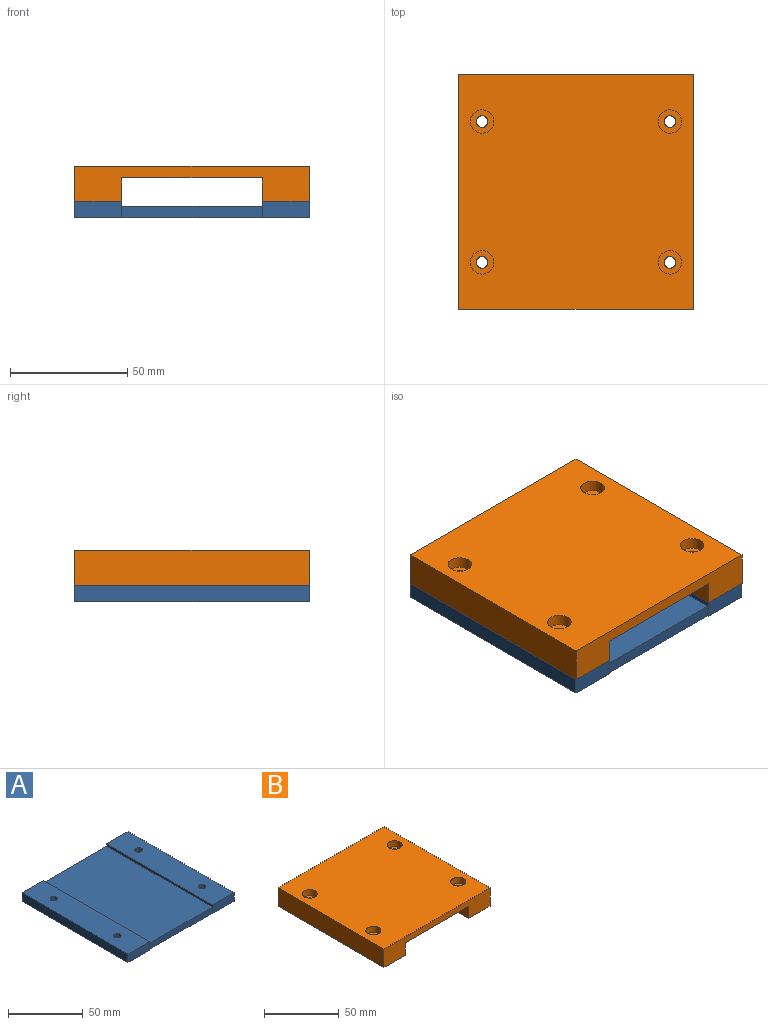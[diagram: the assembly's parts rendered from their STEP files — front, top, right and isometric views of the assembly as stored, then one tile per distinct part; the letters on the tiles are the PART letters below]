
ASSEMBLY  parts=2 mates=1
PART A: 24 faces, bbox 100x100x7 mm
  f0: plane 100x7mm, normal (0,1,0), area 580mm2, adj f2,f3,f4,f5,f7,f8,f10,f11
  f1: plane 60x5mm, normal (0,-1,0), area 300mm2, adj f2,f3,f4,f8
  f2: plane 99.46x60mm, normal (0,0,1), area 5967.6mm2, adj f0,f1,f4,f8
  f3: plane 100x100mm, normal (0,0,-1), area 9653.4mm2, adj f0,f1,f4,f5,f6,f8,f9,f10
  f4: plane 100x7mm, normal (1,0,0), area 202.7mm2, adj f0,f1,f2,f3,f6,f7
  f5: plane 100x7mm, normal (-1,0,0), area 700mm2, adj f0,f3,f6,f7
  f6: plane 20x7mm, normal (0,-1,0), area 140mm2, adj f3,f4,f5,f7
  f7: plane 100x20mm, normal (0,0,1), area 1960.7mm2, adj f0,f4,f5,f6,f12,f15
  f8: plane 100x7mm, normal (-1,0,0), area 202.7mm2, adj f0,f1,f2,f3,f9,f11
  f9: plane 20x7mm, normal (0,-1,0), area 140mm2, adj f3,f8,f10,f11
  f10: plane 100x7mm, normal (1,0,0), area 700mm2, adj f0,f3,f9,f11
  f11: plane 100x20mm, normal (0,0,1), area 1960.7mm2, adj f0,f8,f9,f10,f18,f21
  f12: cylinder r=2.5mm len=5mm, axis (0,0,-1), area 31.4mm2, adj f7,f13
  f13: plane 10x10mm, normal (0,0,-1), area 58.9mm2, adj f12,f14
  f14: cylinder r=5mm len=10mm, axis (0,0,-1), area 157.1mm2, adj f3,f13
  f15: cylinder r=2.5mm len=5mm, axis (0,0,-1), area 31.4mm2, adj f7,f16
  f16: plane 10x10mm, normal (0,0,-1), area 58.9mm2, adj f15,f17
  f17: cylinder r=5mm len=10mm, axis (0,0,-1), area 157.1mm2, adj f3,f16
  f18: cylinder r=2.5mm len=5mm, axis (0,0,-1), area 31.4mm2, adj f11,f19
  f19: plane 10x10mm, normal (0,0,-1), area 58.9mm2, adj f18,f20
  f20: cylinder r=5mm len=10mm, axis (0,0,-1), area 157.1mm2, adj f3,f19
  f21: cylinder r=2.5mm len=5mm, axis (0,0,-1), area 31.4mm2, adj f11,f22
  f22: plane 10x10mm, normal (0,0,-1), area 58.9mm2, adj f21,f23
  f23: cylinder r=5mm len=10mm, axis (0,0,-1), area 157.1mm2, adj f3,f22
PART B: 22 faces, bbox 100x100x15 mm
  f0: plane 100x15mm, normal (0,1,0), area 900mm2, adj f2,f3,f4,f5,f6,f7,f8,f9
  f1: plane 100x15mm, normal (0,-1,0), area 900mm2, adj f2,f3,f4,f5,f6,f7,f8,f9
  f2: plane 100x100mm, normal (0,0,1), area 9685.8mm2, adj f0,f1,f5,f8,f12,f15,f18,f21
  f3: plane 100x60mm, normal (0,0,-1), area 6000mm2, adj f0,f1,f4,f7
  f4: plane 100x10mm, normal (1,0,0), area 1000mm2, adj f0,f1,f3,f6
  f5: plane 100x15mm, normal (-1,0,0), area 1500mm2, adj f0,f1,f2,f6
  f6: plane 100x20mm, normal (0,0,-1), area 1960.7mm2, adj f0,f1,f4,f5,f10,f13
  f7: plane 100x10mm, normal (-1,0,0), area 1000mm2, adj f0,f1,f3,f9
  f8: plane 100x15mm, normal (1,0,0), area 1500mm2, adj f0,f1,f2,f9
  f9: plane 100x20mm, normal (0,0,-1), area 1960.7mm2, adj f0,f1,f7,f8,f16,f19
  f10: cylinder r=2.5mm len=10mm, axis (0,0,1), area 157.1mm2, adj f6,f11
  f11: plane 10x10mm, normal (0,0,1), area 58.9mm2, adj f10,f12
  f12: cylinder r=5mm len=10mm, axis (0,0,1), area 157.1mm2, adj f2,f11
  f13: cylinder r=2.5mm len=10mm, axis (0,0,1), area 157.1mm2, adj f6,f14
  f14: plane 10x10mm, normal (0,0,1), area 58.9mm2, adj f13,f15
  f15: cylinder r=5mm len=10mm, axis (0,0,1), area 157.1mm2, adj f2,f14
  f16: cylinder r=2.5mm len=10mm, axis (0,0,1), area 157.1mm2, adj f9,f17
  f17: plane 10x10mm, normal (0,0,1), area 58.9mm2, adj f16,f18
  f18: cylinder r=5mm len=10mm, axis (0,0,1), area 157.1mm2, adj f2,f17
  f19: cylinder r=2.5mm len=10mm, axis (0,0,1), area 157.1mm2, adj f9,f20
  f20: plane 10x10mm, normal (0,0,1), area 58.9mm2, adj f19,f21
  f21: cylinder r=5mm len=10mm, axis (0,0,1), area 157.1mm2, adj f2,f20
PLACE A t=(-39.3,26.97,-22.92)mm
PLACE B t=(3.69,8.92,-5.92)mm
MATE planar B.f10 <-> A.f12  axis (0,0,-1) through (-79.3,-3.09,-15.92)mm
